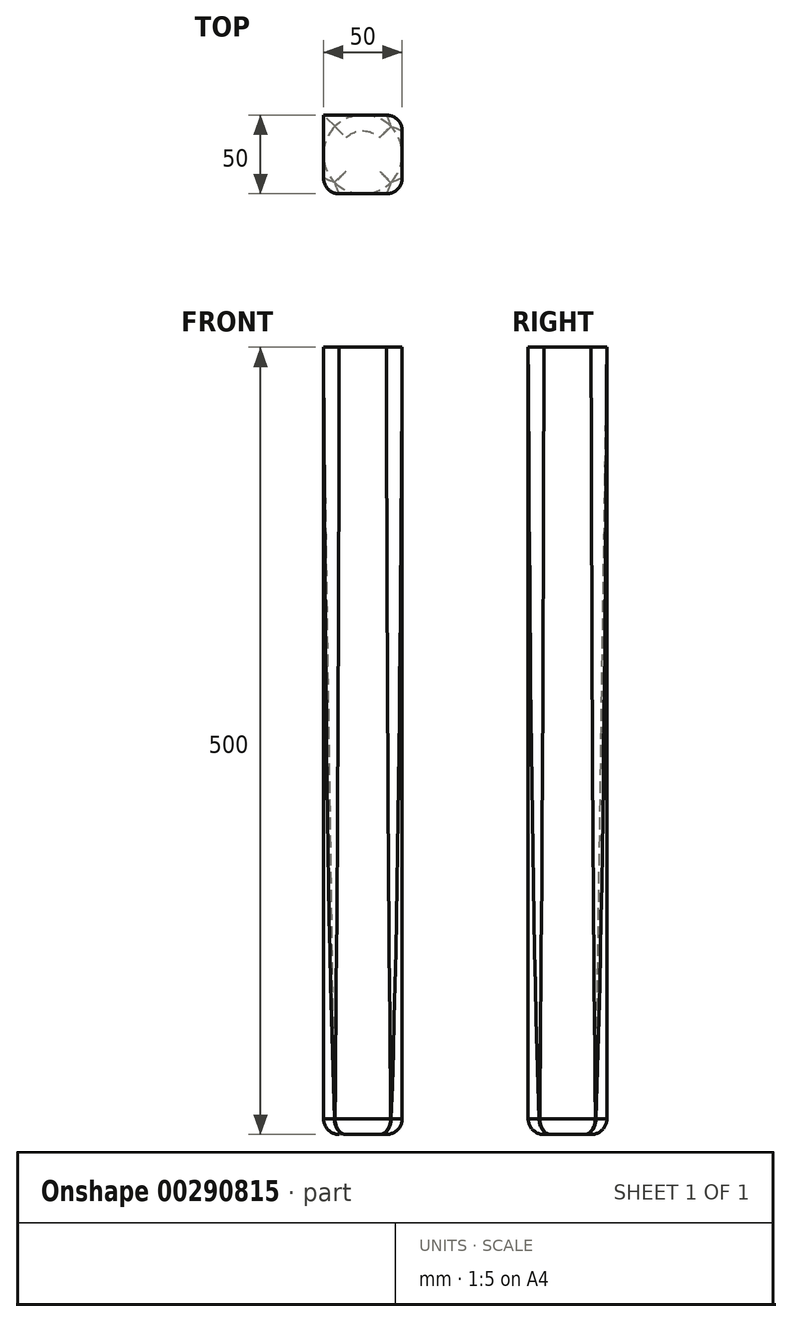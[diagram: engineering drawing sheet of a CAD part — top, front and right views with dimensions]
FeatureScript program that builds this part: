
annotation { "Feature Type Name" : "Feature", "Feature Type Description" : "" }
export const myFeature = defineFeature(function(context is Context, id is Id, definition is map)
    precondition{}
    {
        {
            var Q0;
            Q0=qCreatedBy(makeId("Top.planeOp"),FACE);
            var sketch = newSketch(context, id + "F0", { "sketchPlane" : qUnion([Q0])});
            skCircle(sketch, "E0", {"center": v(0, 0) * mm, "radius": 25 * mm});
            skSolve(sketch);
        }
        {
            var Q0;
            Q0=qCreatedBy(makeId("Top.planeOp"),FACE);
            cPlane(context, id + "F1", {"entities" : qUnion([Q0]), "cplaneType" : CPlaneType.OFFSET, "offset" : 500 * mm, "width" : 150 * mm, "height" : 150 * mm});
        }
        {
            var Q0;
            Q0=qCreatedBy(id+"F1.planeOp",FACE);
            var sketch = newSketch(context, id + "F2", { "sketchPlane" : qUnion([Q0])});
            skLineSegment(sketch, "E1.bottom", {"start": v(25, 25) * mm, "end": v(-25, 25) * mm});
            skLineSegment(sketch, "E1.top", {"start": v(25, -25) * mm, "end": v(-25, -25) * mm});
            skLineSegment(sketch, "E1.left", {"start": v(25, 25) * mm, "end": v(25, -25) * mm});
            skLineSegment(sketch, "E1.right", {"start": v(-25, 25) * mm, "end": v(-25, -25) * mm});
            skPoint(sketch, "E1.middle", {"position": v(0, 0) * mm});
            skSolve(sketch);
        }
        {
            var Q0;
            Q0=makeQuery(id+"F0.imprint","IMPRINT",FACE,{"disambiguationData":[TD([[makeQuery(id+"F0.imprint","IMPRINT",EDGE,{"derivedFrom":sQuery(id+"F0.wireOp",EDGE,"E0")}),1.0]])]});
            var Q1;
            Q1=makeQuery(id+"F2.imprint","IMPRINT",FACE,{"disambiguationData":[TD([[makeQuery(id+"F2.imprint","IMPRINT",EDGE,{"derivedFrom":sQuery(id+"F2.wireOp",EDGE,"E1.bottom")}),1.0]])]});
            loft(context, id + "F3", {"sheetProfilesArray" : [{ "sheetProfileEntities" : qUnion([Q0]) }, { "sheetProfileEntities" : qUnion([Q1]) }]});
        }
        {
            var Q0;
            Q0=makeQuery(id+"F3.opLoft","SWEPT_EDGE",EDGE,{"disambiguationData":[OSD([sQuery(id+"F0.wireOp",EDGE,"E0"),sQuery(id+"F2.wireOp",EDGE,"E1.top"),sQuery(id+"F2.wireOp",EDGE,"E1.left"),sQuery(id+"F2.wireOp",EDGE,"E1.right")])]});
            var Q1;
            Q1=makeQuery(id+"F3.opLoft","SWEPT_EDGE",EDGE,{"disambiguationData":[OSD([sQuery(id+"F2.wireOp",EDGE,"E1.bottom"),sQuery(id+"F2.wireOp",EDGE,"E1.left")])]});
            var Q2;
            Q2=makeQuery(id+"F3.opLoft","SWEPT_EDGE",EDGE,{"disambiguationData":[OSD([sQuery(id+"F0.wireOp",EDGE,"E0"),sQuery(id+"F2.wireOp",EDGE,"E1.bottom"),sQuery(id+"F2.wireOp",EDGE,"E1.left"),sQuery(id+"F2.wireOp",EDGE,"E1.right")])]});
            var Q3;
            Q3=makeQuery(id+"F3.opLoft","SWEPT_EDGE",EDGE,{"disambiguationData":[OSD([sQuery(id+"F0.wireOp",EDGE,"E0"),sQuery(id+"F2.wireOp",EDGE,"E1.bottom"),sQuery(id+"F2.wireOp",EDGE,"E1.top"),sQuery(id+"F2.wireOp",EDGE,"E1.right")])]});
            var Q4;
            Q4=makeQuery(id+"F3.opLoft","MID_CAP_EDGE",EDGE,{"disambiguationData":[OSD([sQuery(id+"F0.wireOp",EDGE,"E0"),sQuery(id+"F2.wireOp",EDGE,"E1.bottom"),sQuery(id+"F2.wireOp",EDGE,"E1.left"),sQuery(id+"F2.wireOp",EDGE,"E1.right")])],"capPos":0.0});
            var Q5;
            Q5=makeQuery(id+"F3.opLoft","MID_CAP_EDGE",EDGE,{"disambiguationData":[OSD([sQuery(id+"F0.wireOp",EDGE,"E0"),sQuery(id+"F2.wireOp",EDGE,"E1.bottom"),sQuery(id+"F2.wireOp",EDGE,"E1.left")])],"capPos":0.0});
            var Q6;
            Q6=makeQuery(id+"F3.opLoft","MID_CAP_EDGE",EDGE,{"disambiguationData":[OSD([sQuery(id+"F0.wireOp",EDGE,"E0"),sQuery(id+"F2.wireOp",EDGE,"E1.bottom"),sQuery(id+"F2.wireOp",EDGE,"E1.top"),sQuery(id+"F2.wireOp",EDGE,"E1.left"),sQuery(id+"F2.wireOp",EDGE,"E1.right")])],"capPos":0.0});
            var Q7;
            Q7=makeQuery(id+"F3.opLoft","MID_CAP_EDGE",EDGE,{"disambiguationData":[OSD([sQuery(id+"F0.wireOp",EDGE,"E0"),sQuery(id+"F2.wireOp",EDGE,"E1.bottom"),sQuery(id+"F2.wireOp",EDGE,"E1.top"),sQuery(id+"F2.wireOp",EDGE,"E1.right")])],"capPos":0.0});
            fillet(context, id + "F4", {"entities" : qUnion([Q0, Q1, Q2, Q3, Q4, Q5, Q6, Q7]), "radius" : 10 * mm, "tangentPropagation" : true, "allowEdgeOverflow" : false});
        }
    });
